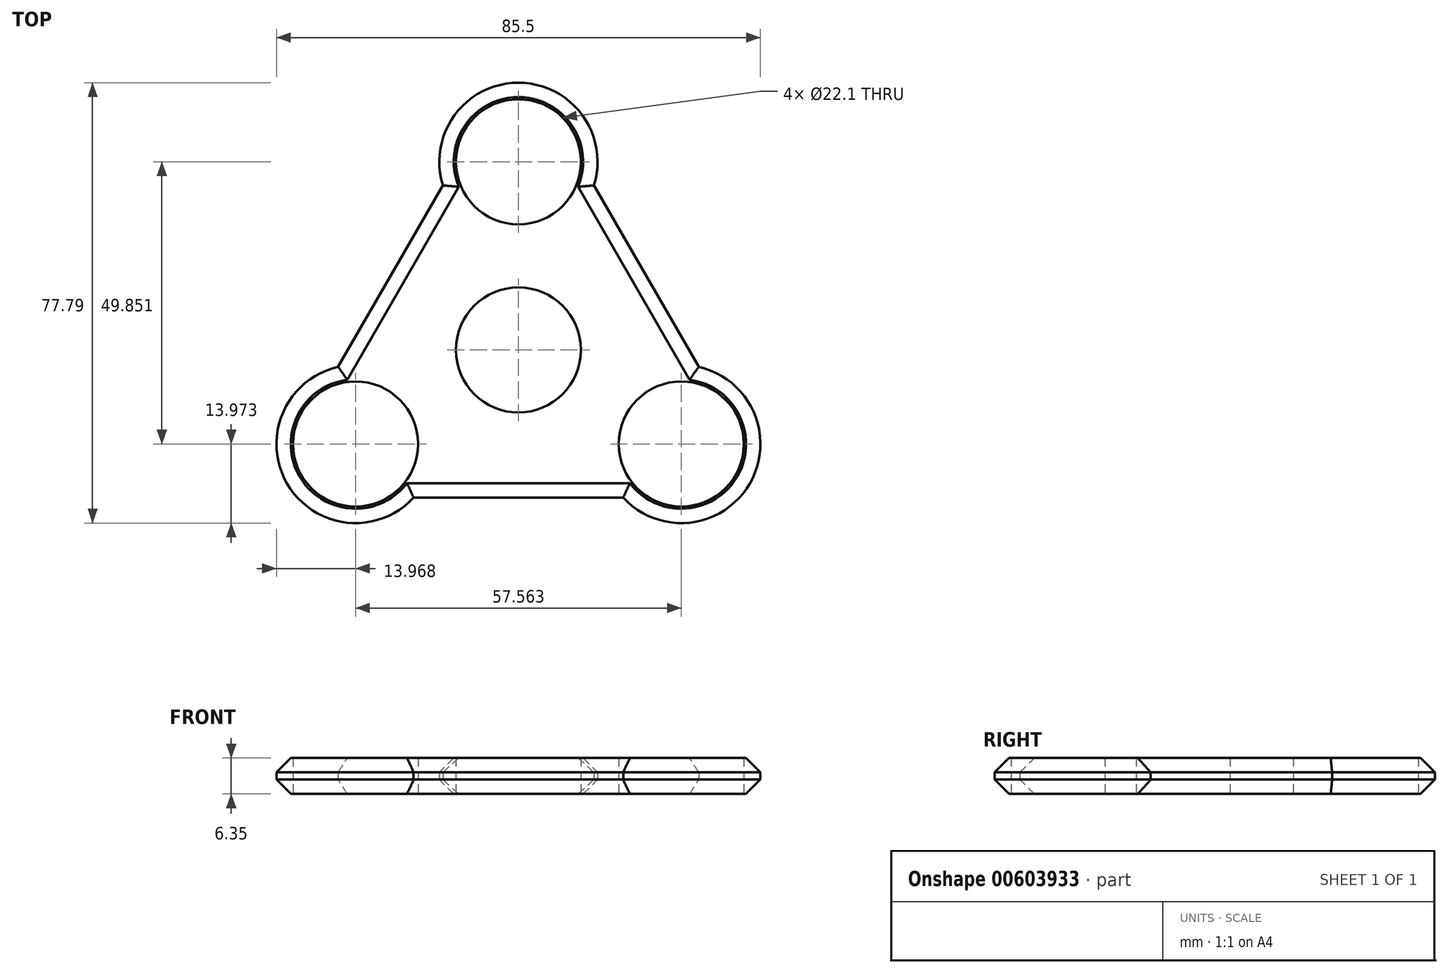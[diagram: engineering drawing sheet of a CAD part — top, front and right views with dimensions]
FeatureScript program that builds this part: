
annotation { "Feature Type Name" : "Feature", "Feature Type Description" : "" }
export const myFeature = defineFeature(function(context is Context, id is Id, definition is map)
    precondition{}
    {
        {
            var Q0;
            Q0=qCreatedBy(makeId("Top.planeOp"),FACE);
            var sketch = newSketch(context, id + "F0", { "sketchPlane" : qUnion([Q0])});
            skCircle(sketch, "E0", {"center": v(0, 0) * mm, "radius": 11.05 * mm});
            skCircle(sketch, "E1", {"center": v(0, 0) * mm, "radius": 13.97 * mm});
            skLineSegment(sketch, "E2", {"start": v(0, -2.33) * mm, "end": v(0, 33.23) * mm});
            skCircle(sketch, "E3", {"center": v(0, 33.23) * mm, "radius": 11.05 * mm});
            skCircle(sketch, "E4", {"center": v(0, 33.23) * mm, "radius": 13.97 * mm});
            skCircle(sketch, "E5.1.0", {"center": v(-28.78, -16.62) * mm, "radius": 11.05 * mm});
            skCircle(sketch, "E5.1.1", {"center": v(-28.78, -16.62) * mm, "radius": 13.97 * mm});
            skCircle(sketch, "E5.2.0", {"center": v(28.78, -16.62) * mm, "radius": 11.05 * mm});
            skCircle(sketch, "E5.2.1", {"center": v(28.78, -16.62) * mm, "radius": 13.97 * mm});
            skArc(sketch, "E6", {"start": v(-31.85, -2.99) * mm, "mid": v(-15.57, 9) * mm, "end": v(-13.34, 29.08) * mm});
            skArc(sketch, "E7.1.0", {"start": v(18.52, -26.1) * mm, "mid": v(0, -17.98) * mm, "end": v(-18.52, -26.1) * mm});
            skArc(sketch, "E7.2.0", {"start": v(13.34, 29.08) * mm, "mid": v(15.57, 9) * mm, "end": v(31.85, -2.99) * mm});
            skLineSegment(sketch, "E8", {"start": v(-13.34, 29.08) * mm, "end": v(-31.85, -2.99) * mm});
            skLineSegment(sketch, "E9", {"start": v(-18.52, -26.1) * mm, "end": v(18.52, -26.1) * mm});
            skLineSegment(sketch, "E10", {"start": v(31.85, -2.99) * mm, "end": v(13.34, 29.08) * mm});
            skSolve(sketch);
        }
        {
            var Q0;
            Q0 = qSketchRegion(id + "F0", true);
            extrude(context, id + "F1", {"entities" : qUnion([Q0]), "depth" : 6.35 * mm, "offsetDistance" : 25.4 * mm});
        }
        {
            var Q0;
            Q0=makeQuery(id+"F1.opExtrude","CAP_EDGE",EDGE,{"disambiguationData":[OSD([sQuery(id+"F0.wireOp",EDGE,"E9")])],"isStart":false});
            var Q1;
            Q1=makeQuery(id+"F1.opExtrude","CAP_EDGE",EDGE,{"disambiguationData":[OSD([sQuery(id+"F0.wireOp",EDGE,"E8")])],"isStart":false});
            var Q2;
            Q2=makeQuery(id+"F1.opExtrude","CAP_EDGE",EDGE,{"disambiguationData":[OSD([sQuery(id+"F0.wireOp",EDGE,"E10")])],"isStart":false});
            var Q3;
            Q3=makeQuery(id+"F1.opExtrude","CAP_EDGE",EDGE,{"disambiguationData":[OSD([sQuery(id+"F0.wireOp",EDGE,"E5.1.1")])],"isStart":false});
            var Q4;
            Q4=makeQuery(id+"F1.opExtrude","CAP_EDGE",EDGE,{"disambiguationData":[OSD([sQuery(id+"F0.wireOp",EDGE,"E5.2.1")])],"isStart":false});
            var Q5;
            Q5=makeQuery(id+"F1.opExtrude","CAP_EDGE",EDGE,{"disambiguationData":[OSD([sQuery(id+"F0.wireOp",EDGE,"E4")])],"isStart":false});
            var Q6;
            Q6=makeQuery(id+"F1.opExtrude","CAP_EDGE",EDGE,{"disambiguationData":[OSD([sQuery(id+"F0.wireOp",EDGE,"E4")])],"isStart":true});
            var Q7;
            Q7=makeQuery(id+"F1.opExtrude","CAP_EDGE",EDGE,{"disambiguationData":[OSD([sQuery(id+"F0.wireOp",EDGE,"E8")])],"isStart":true});
            var Q8;
            Q8=makeQuery(id+"F1.opExtrude","CAP_EDGE",EDGE,{"disambiguationData":[OSD([sQuery(id+"F0.wireOp",EDGE,"E5.1.1")])],"isStart":true});
            var Q9;
            Q9=makeQuery(id+"F1.opExtrude","CAP_EDGE",EDGE,{"disambiguationData":[OSD([sQuery(id+"F0.wireOp",EDGE,"E9")])],"isStart":true});
            var Q10;
            Q10=makeQuery(id+"F1.opExtrude","CAP_EDGE",EDGE,{"disambiguationData":[OSD([sQuery(id+"F0.wireOp",EDGE,"E5.2.1")])],"isStart":true});
            var Q11;
            Q11=makeQuery(id+"F1.opExtrude","CAP_EDGE",EDGE,{"disambiguationData":[OSD([sQuery(id+"F0.wireOp",EDGE,"E10")])],"isStart":true});
            chamfer(context, id + "F2", {"entities" : qUnion([Q0, Q1, Q2, Q3, Q4, Q5, Q6, Q7, Q8, Q9, Q10, Q11]), "width" : 2.54 * mm, "tangentPropagation" : true});
        }
        {
            var Q0;
            Q0=makeQuery(id+"F0.imprint","IMPRINT",FACE,{"disambiguationData":[TD([[makeQuery(id+"F0.imprint","IMPRINT",EDGE,{"derivedFrom":sQuery(id+"F0.wireOp",EDGE,"E0")}),-1.0]])]});
            extrude(context, id + "F3", {"entities" : qUnion([Q0]), "operationType" : NewBodyOperationType.ADD, "depth" : 6.35 * mm, "offsetDistance" : 25.4 * mm});
        }
    });
